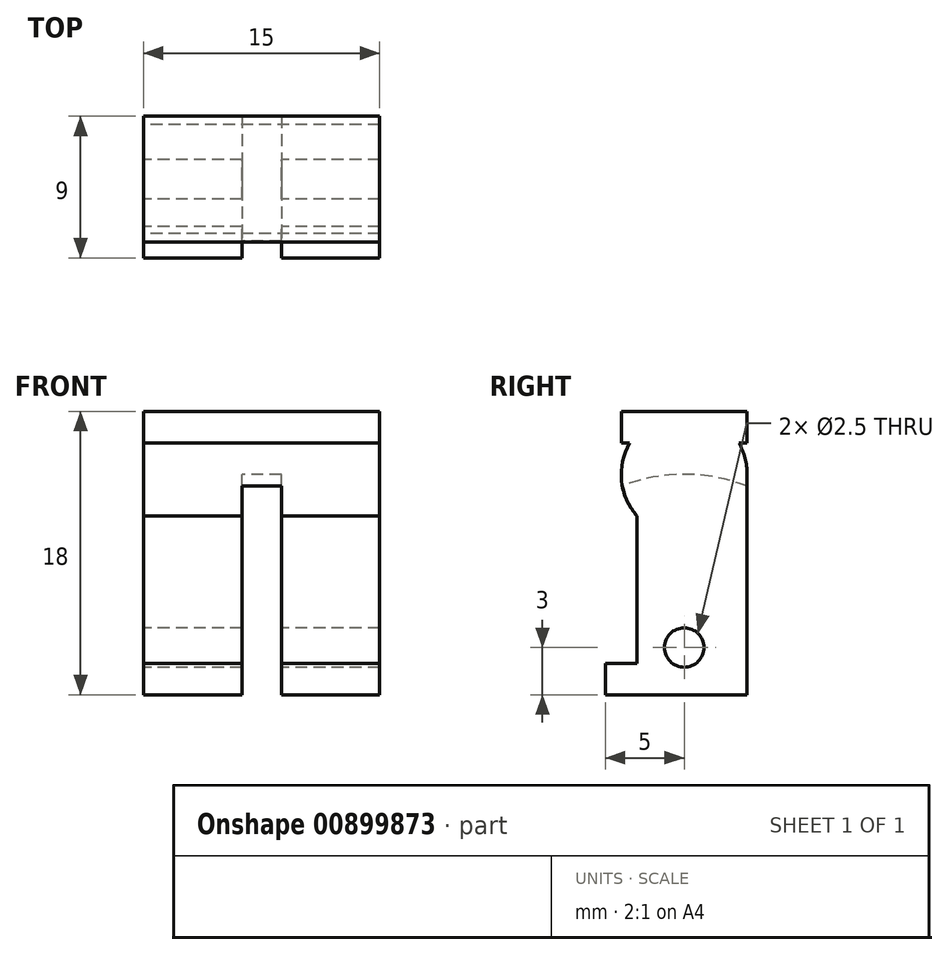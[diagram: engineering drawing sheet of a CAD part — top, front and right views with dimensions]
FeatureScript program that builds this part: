
annotation { "Feature Type Name" : "Feature", "Feature Type Description" : "" }
export const myFeature = defineFeature(function(context is Context, id is Id, definition is map)
    precondition{}
    {
        {
            var Q0;
            Q0=qCreatedBy(makeId("Right.planeOp"),FACE);
            var sketch = newSketch(context, id + "F0", { "sketchPlane" : qUnion([Q0])});
            skLineSegment(sketch, "E0.bottom", {"start": v(4, -1) * mm, "end": v(3.46, -1) * mm});
            skLineSegment(sketch, "E0.top", {"start": v(4, 1) * mm, "end": v(-4, 1) * mm});
            skLineSegment(sketch, "E0.left", {"start": v(4, -1) * mm, "end": v(4, 1) * mm});
            skLineSegment(sketch, "E0.right", {"start": v(-4, -1) * mm, "end": v(-4, 1) * mm});
            skPoint(sketch, "E0.middle", {"position": v(0, 0) * mm});
            skArc(sketch, "E1", {"start": v(-3.46, -1) * mm, "mid": v(-3.98, -3.4) * mm, "end": v(-3, -5.65) * mm});
            skLineSegment(sketch, "E2.left", {"start": v(4, -15) * mm, "end": v(4, -3) * mm});
            skLineSegment(sketch, "E2.right", {"start": v(-3, -15) * mm, "end": v(-3, -5.65) * mm});
            skLineSegment(sketch, "E3.top", {"start": v(4, -17) * mm, "end": v(-5, -17) * mm});
            skLineSegment(sketch, "E3.left", {"start": v(4, -15) * mm, "end": v(4, -17) * mm});
            skLineSegment(sketch, "E3.right", {"start": v(-5, -15) * mm, "end": v(-5, -17) * mm});
            skCircle(sketch, "E4", {"center": v(0, -14) * mm, "radius": 1.25 * mm});
            skArc(sketch, "E5.trimOffspring", {"start": v(4, -3) * mm, "mid": v(3.86, -1.96) * mm, "end": v(3.46, -1) * mm});
            skLineSegment(sketch, "E6.trimOffspring", {"start": v(-3.46, -1) * mm, "end": v(-4, -1) * mm});
            skLineSegment(sketch, "E7.trimOffspring", {"start": v(-3, -15) * mm, "end": v(-5, -15) * mm});
            skSolve(sketch);
        }
        {
            var Q0;
            Q0 = qSketchRegion(id + "F0", true);
            extrude(context, id + "F1", {"entities" : qUnion([Q0]), "endBound" : BoundingType.SYMMETRIC, "depth" : 15 * mm, "offsetDistance" : 25.4 * mm});
        }
        {
            var Q0;
            Q0=qCreatedBy(makeId("Right.planeOp"),FACE);
            var sketch = newSketch(context, id + "F2", { "sketchPlane" : qUnion([Q0])});
            skCircle(sketch, "E8", {"center": v(0, -14) * mm, "radius": 11 * mm});
            skSolve(sketch);
        }
        {
            var Q0;
            Q0 = qSketchRegion(id + "F2", true);
            extrude(context, id + "F3", {"entities" : qUnion([Q0]), "operationType" : NewBodyOperationType.REMOVE, "endBound" : BoundingType.SYMMETRIC, "depth" : 2.5 * mm, "offsetDistance" : 25.4 * mm});
        }
    });
